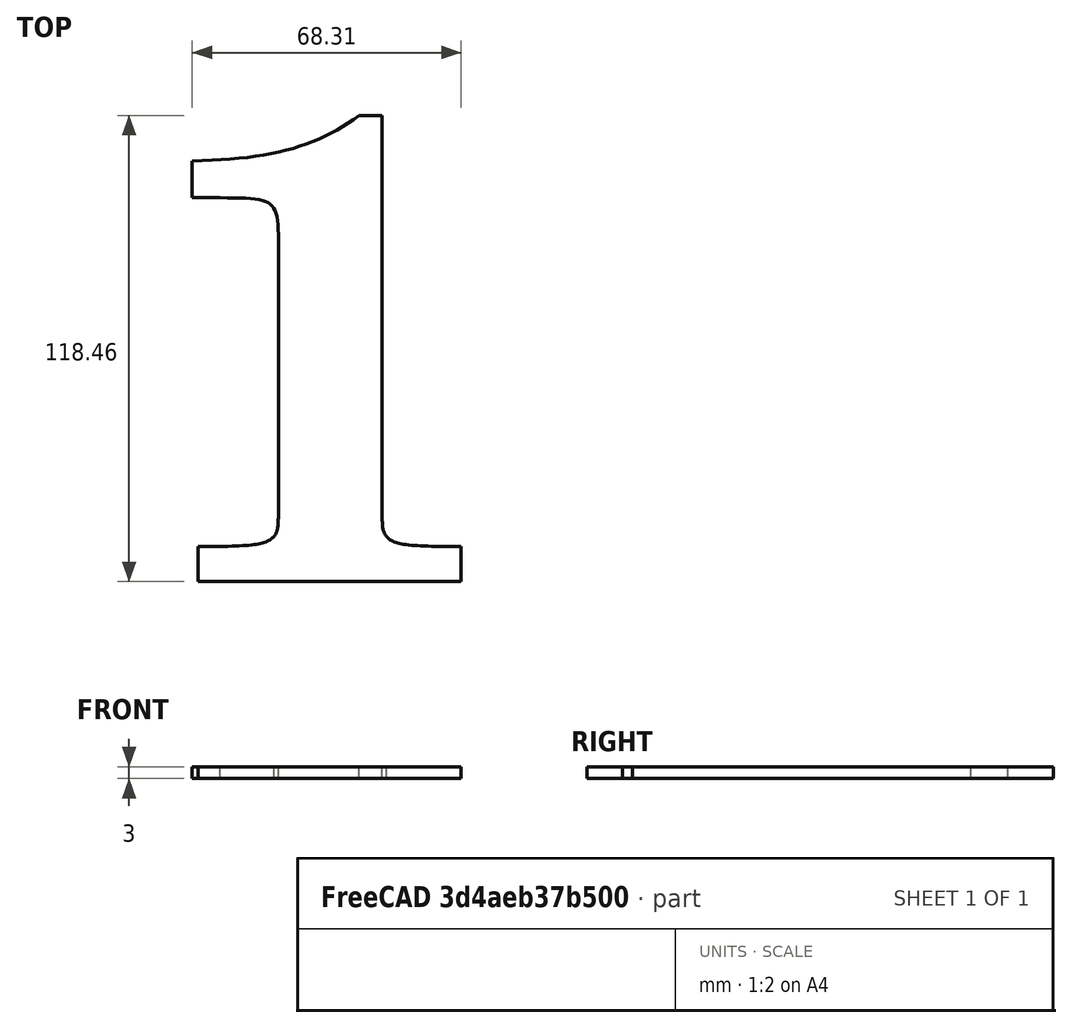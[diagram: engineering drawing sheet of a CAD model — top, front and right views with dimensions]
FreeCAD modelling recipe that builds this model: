
FCSTD DOCUMENT  (FreeCAD 0.20R29603 (Git))
Label: numero-uno
License: All rights reserved
LicenseURL: http://en.wikipedia.org/wiki/All_rights_reserved
objects: Part::Part2DObjectPython×1, PartDesign::Pad×1, PartDesign::Body×1, App::MeasureDistance×1
note: 4 computed .brp shape members not serialized (recipe doc carries the construction recipe); baked Part::Feature solids carry a one-line shape summary decoded from their .brp

FEATURE [Part::Part2DObjectPython] ShapeString  # Draft 2D object (typed FeaturePython)
  FontFile = <path>
  MakeFace = true
  Size = 75
  String = 1
  Tracking = 0
FEATURE [PartDesign::Pad] Pad
  Direction = (0,0,1)
  Length = 3
  Length2 = 10
  Profile = -> ShapeString
  ReferenceAxis = -> ShapeString [N_Axis]
  Type = 0
FEATURE [PartDesign::Body] Body
  Group = -> [ShapeString,Pad]
  Origin = -> Origin
  Tip = -> Pad
FEATURE [App::MeasureDistance] Distance  label="Distance: 118.47 mm"
  Distance = 118.467
  P1 = (62.037,118.464,3)
  P2 = (62.8335,0,3)
note: 1 file-system path scrubbed to <path> (originals preserved in the JSON sidecar)
